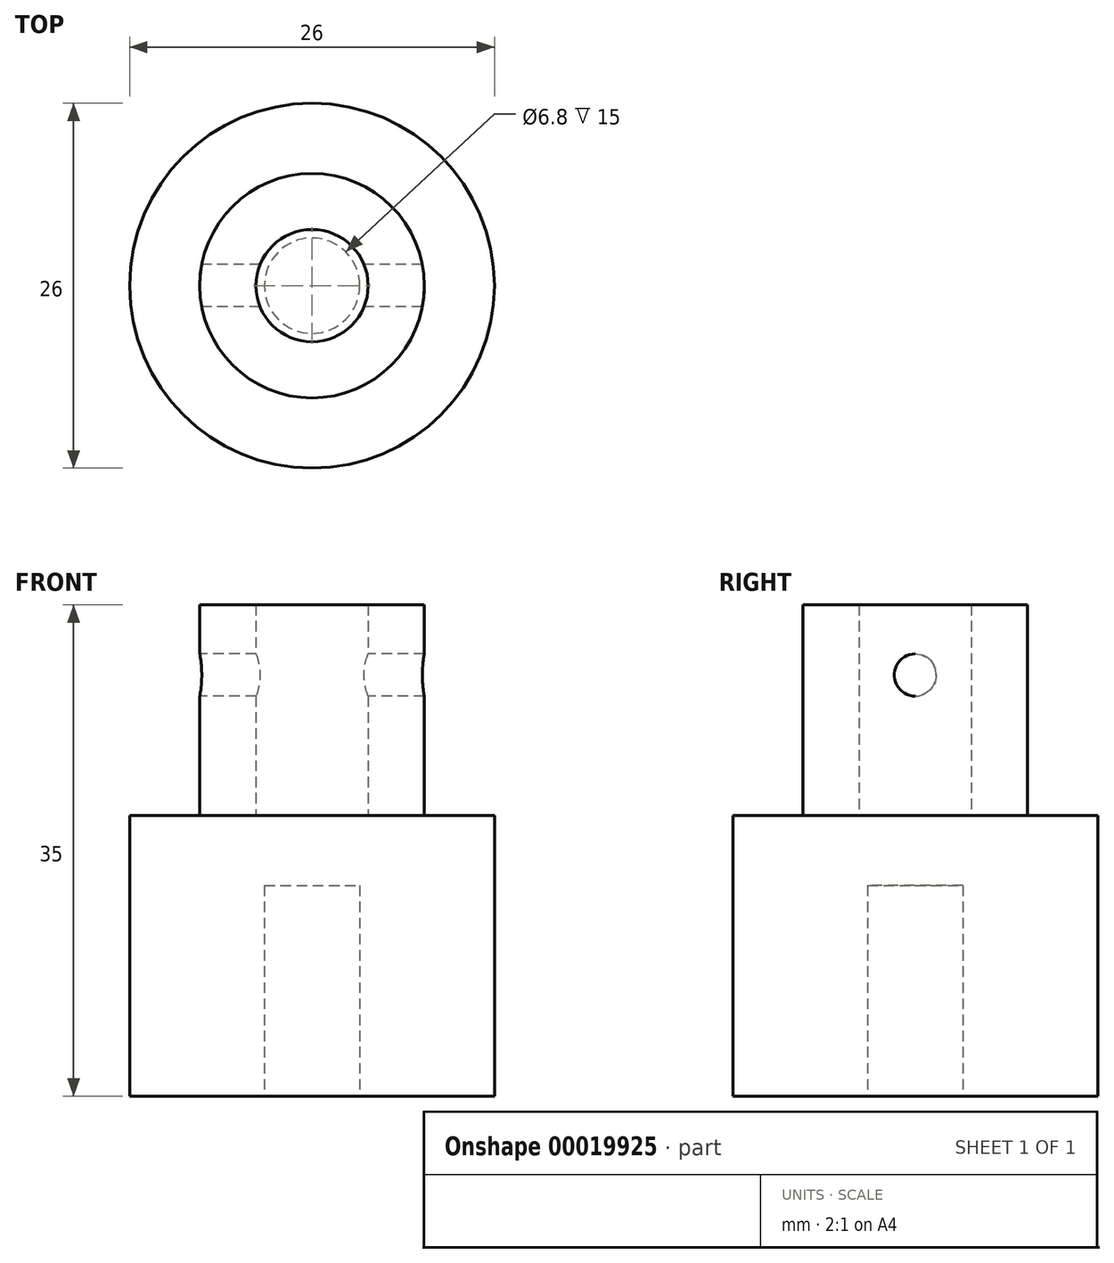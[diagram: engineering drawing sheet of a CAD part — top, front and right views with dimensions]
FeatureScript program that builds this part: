
annotation { "Feature Type Name" : "Feature", "Feature Type Description" : "" }
export const myFeature = defineFeature(function(context is Context, id is Id, definition is map)
    precondition{}
    {
        {
            var Q0;
            Q0=qCreatedBy(makeId("Top.planeOp"),FACE);
            var sketch = newSketch(context, id + "F0", { "sketchPlane" : qUnion([Q0])});
            skCircle(sketch, "E0", {"center": v(0, 0) * mm, "radius": 4 * mm});
            skCircle(sketch, "E1", {"center": v(0, 0) * mm, "radius": 8 * mm});
            skCircle(sketch, "E2", {"center": v(0, 0) * mm, "radius": 13 * mm});
            skSolve(sketch);
        }
        {
            var Q0;
            Q0=makeQuery(id+"F0.imprint","IMPRINT",FACE,{"disambiguationData":[TD([[makeQuery(id+"F0.imprint","IMPRINT",EDGE,{"derivedFrom":sQuery(id+"F0.wireOp",EDGE,"E0")}),1.0]])]});
            extrude(context, id + "F1", {"entities" : qUnion([Q0]), "depth" : 20 * mm});
        }
        {
            var Q0;
            Q0=makeQuery(id+"F0.imprint","IMPRINT",FACE,{"disambiguationData":[TD([[makeQuery(id+"F0.imprint","IMPRINT",EDGE,{"derivedFrom":sQuery(id+"F0.wireOp",EDGE,"E0")}),-1.0]])]});
            extrude(context, id + "F2", {"entities" : qUnion([Q0]), "operationType" : NewBodyOperationType.ADD, "depth" : 35 * mm});
        }
        {
            var Q0;
            Q0=makeQuery(id+"F0.imprint","IMPRINT",FACE,{"disambiguationData":[TD([[makeQuery(id+"F0.imprint","IMPRINT",EDGE,{"derivedFrom":sQuery(id+"F0.wireOp",EDGE,"E1")}),-1.0]])]});
            extrude(context, id + "F3", {"entities" : qUnion([Q0]), "operationType" : NewBodyOperationType.ADD, "depth" : 20 * mm});
        }
        {
            var Q0;
            {var subQ0=sQuery(id+"F0.wireOp",EDGE,"E0");var subQ1=sQuery(id+"F0.wireOp",EDGE,"E1");Q0=makeQuery(id+"F3.boolean.opBoolean","MERGE",FACE,{"derivedFrom":[makeQuery(id+"F2.boolean.opBoolean","MERGE",FACE,{"derivedFrom":[makeQuery(id+"F1.opExtrude","CAP_FACE",FACE,{"disambiguationData":[OSD([subQ0])],"isStart":true}),makeQuery(id+"F2.opExtrude","CAP_FACE",FACE,{"disambiguationData":[OSD([subQ0,subQ1])],"isStart":true})]}),makeQuery(id+"F3.opExtrude","CAP_FACE",FACE,{"disambiguationData":[OSD([subQ1,sQuery(id+"F0.wireOp",EDGE,"E2")])],"isStart":true})]});}
            var sketch = newSketch(context, id + "F4", { "sketchPlane" : qUnion([Q0])});
            skCircle(sketch, "E3", {"center": v(0, 0) * mm, "radius": 3.4 * mm});
            skSolve(sketch);
        }
        {
            var Q0;
            Q0 = qSketchRegion(id + "F4", true);
            extrude(context, id + "F5", {"entities" : qUnion([Q0]), "operationType" : NewBodyOperationType.REMOVE, "oppositeDirection" : true, "depth" : 15 * mm});
        }
        {
            var Q0;
            Q0=qCreatedBy(makeId("Right.planeOp"),FACE);
            var sketch = newSketch(context, id + "F6", { "sketchPlane" : qUnion([Q0])});
            skLineSegment(sketch, "E4", {"start": v(-8, 20) * mm, "end": v(-8, 35) * mm});
            skLineSegment(sketch, "E5", {"start": v(8, 35) * mm, "end": v(8, 20) * mm});
            skCircle(sketch, "E6", {"center": v(0, 30) * mm, "radius": 1.5 * mm});
            skLineSegment(sketch, "E7", {"start": v(-8, 35) * mm, "end": v(8, 35) * mm, "construction": true});
            skLineSegment(sketch, "E8", {"start": v(0, 35) * mm, "end": v(0, 30) * mm, "construction": true});
            skSolve(sketch);
        }
        {
            var Q0;
            Q0 = qSketchRegion(id + "F6", true);
            extrude(context, id + "F7", {"entities" : qUnion([Q0]), "operationType" : NewBodyOperationType.REMOVE, "depth" : 25 * mm, "hasSecondDirection" : true, "secondDirectionOppositeDirection" : true, "secondDirectionDepth" : 25 * mm});
        }
    });
